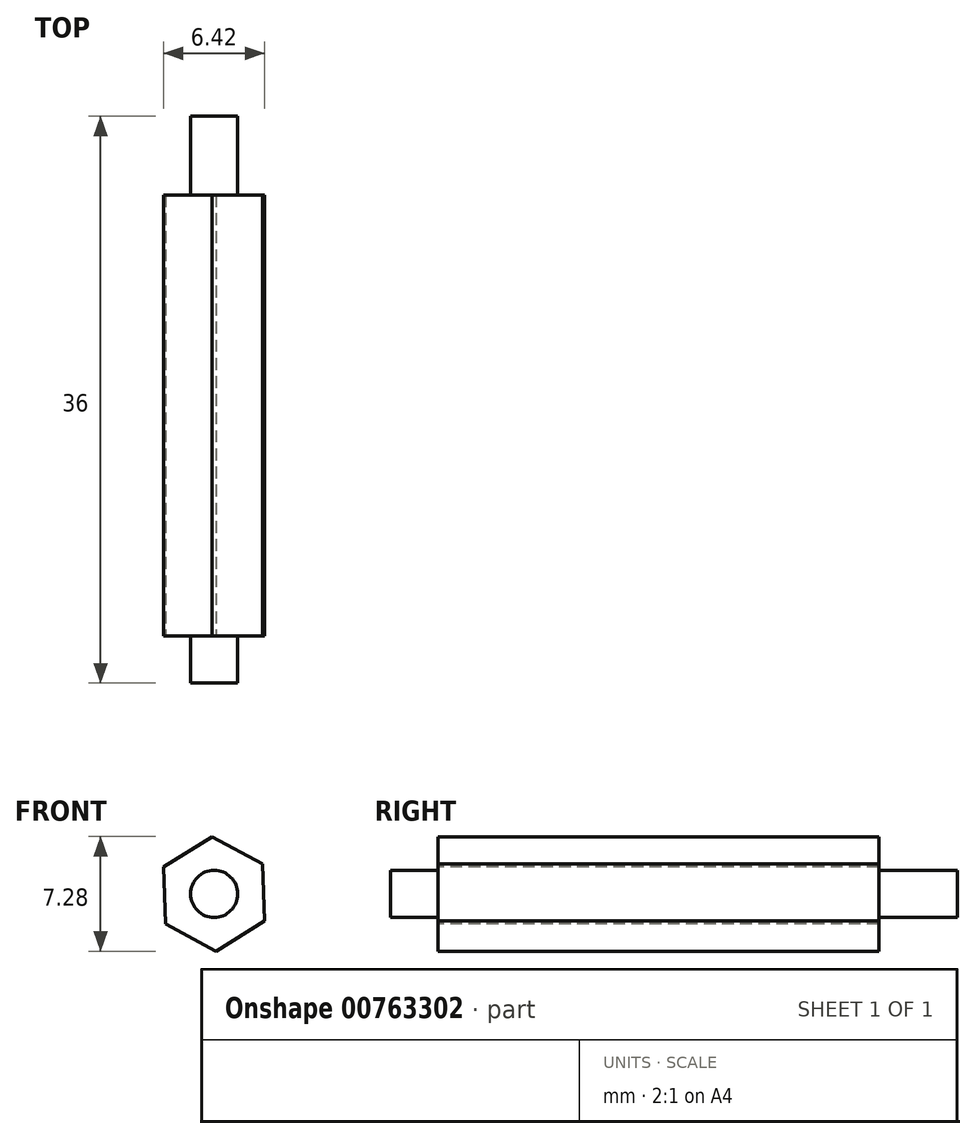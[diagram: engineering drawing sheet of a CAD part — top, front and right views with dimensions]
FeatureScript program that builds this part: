
annotation { "Feature Type Name" : "Feature", "Feature Type Description" : "" }
export const myFeature = defineFeature(function(context is Context, id is Id, definition is map)
    precondition{}
    {
        {
            var Q0;
            Q0=qCreatedBy(makeId("Front.planeOp"),FACE);
            var sketch = newSketch(context, id + "F0", { "sketchPlane" : qUnion([Q0])});
            skCircle(sketch, "E0.cCircle", {"center": v(0, 0) * mm, "radius": 3.64 * mm, "construction": true});
            skLineSegment(sketch, "E0.0", {"start": v(3.2, -1.72) * mm, "end": v(0.12, -3.64) * mm});
            skLineSegment(sketch, "E0.1", {"start": v(0.12, -3.64) * mm, "end": v(-3.1, -1.92) * mm});
            skLineSegment(sketch, "E0.2", {"start": v(-3.1, -1.92) * mm, "end": v(-3.2, 1.72) * mm});
            skLineSegment(sketch, "E0.3", {"start": v(-3.2, 1.72) * mm, "end": v(-0.12, 3.64) * mm});
            skLineSegment(sketch, "E0.4", {"start": v(-0.12, 3.64) * mm, "end": v(3.1, 1.92) * mm});
            skLineSegment(sketch, "E0.5", {"start": v(3.1, 1.92) * mm, "end": v(3.2, -1.72) * mm});
            skSolve(sketch);
        }
        {
            var Q0;
            Q0=makeQuery(id+"F0.imprint","IMPRINT",FACE,{"disambiguationData":[TD([[makeQuery(id+"F0.imprint","IMPRINT",EDGE,{"derivedFrom":sQuery(id+"F0.wireOp",EDGE,"E0.0")}),-1.0]])]});
            extrude(context, id + "F1", {"entities" : qUnion([Q0]), "oppositeDirection" : true, "depth" : 28 * mm, "offsetDistance" : 25 * mm});
        }
        {
            var Q0;
            Q0=makeQuery(id+"F1.opExtrude","CAP_FACE",FACE,{"disambiguationData":[OSD([sQuery(id+"F0.wireOp",EDGE,"E0.0"),sQuery(id+"F0.wireOp",EDGE,"E0.1"),sQuery(id+"F0.wireOp",EDGE,"E0.2"),sQuery(id+"F0.wireOp",EDGE,"E0.3"),sQuery(id+"F0.wireOp",EDGE,"E0.4"),sQuery(id+"F0.wireOp",EDGE,"E0.5")])],"isStart":true});
            var sketch = newSketch(context, id + "F2", { "sketchPlane" : qUnion([Q0])});
            skCircle(sketch, "E1", {"center": v(0, 0) * mm, "radius": 1.5 * mm});
            skSolve(sketch);
        }
        {
            var Q0;
            Q0=makeQuery(id+"F2.imprint","IMPRINT",FACE,{"disambiguationData":[TD([[makeQuery(id+"F2.imprint","IMPRINT",EDGE,{"derivedFrom":sQuery(id+"F2.wireOp",EDGE,"E1")}),1.0]])]});
            extrude(context, id + "F3", {"entities" : qUnion([Q0]), "operationType" : NewBodyOperationType.ADD, "depth" : 3 * mm, "offsetDistance" : 25 * mm});
        }
        {
            var Q0;
            Q0=makeQuery(id+"F1.opExtrude","CAP_FACE",FACE,{"disambiguationData":[OSD([sQuery(id+"F0.wireOp",EDGE,"E0.0"),sQuery(id+"F0.wireOp",EDGE,"E0.1"),sQuery(id+"F0.wireOp",EDGE,"E0.2"),sQuery(id+"F0.wireOp",EDGE,"E0.3"),sQuery(id+"F0.wireOp",EDGE,"E0.4"),sQuery(id+"F0.wireOp",EDGE,"E0.5")])],"isStart":false});
            var sketch = newSketch(context, id + "F4", { "sketchPlane" : qUnion([Q0])});
            skCircle(sketch, "E2", {"center": v(0, 0) * mm, "radius": 1.5 * mm});
            skSolve(sketch);
        }
        {
            var Q0;
            Q0=makeQuery(id+"F4.imprint","IMPRINT",FACE,{"disambiguationData":[TD([[makeQuery(id+"F4.imprint","IMPRINT",EDGE,{"derivedFrom":sQuery(id+"F4.wireOp",EDGE,"E2")}),1.0]])]});
            extrude(context, id + "F5", {"entities" : qUnion([Q0]), "operationType" : NewBodyOperationType.ADD, "depth" : 5 * mm, "offsetDistance" : 25 * mm});
        }
    });
